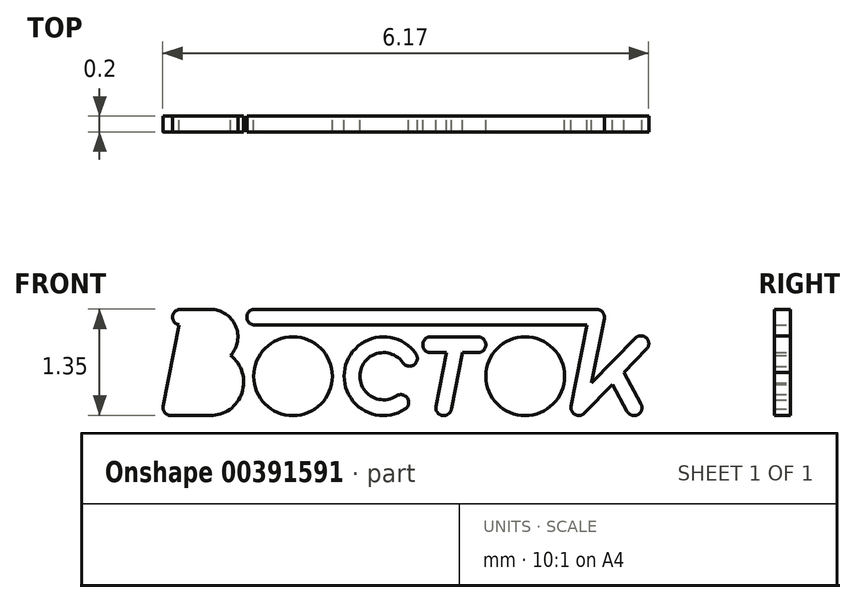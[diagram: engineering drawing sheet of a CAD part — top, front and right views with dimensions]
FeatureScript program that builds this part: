
annotation { "Feature Type Name" : "Feature", "Feature Type Description" : "" }
export const myFeature = defineFeature(function(context is Context, id is Id, definition is map)
    precondition{}
    {
        {
            var Q0;
            Q0=qCreatedBy(makeId("Front.planeOp"),FACE);
            var sketch = newSketch(context, id + "F0", { "sketchPlane" : qUnion([Q0])});
            skArc(sketch, "E0", {"start": v(-21.74, -11.75) * mm, "mid": v(-21.84, -11.84) * mm, "end": v(-21.76, -11.95) * mm});
            skCircle(sketch, "E1", {"center": v(-20.32, -12.6) * mm, "radius": 0.5 * mm});
            skCircle(sketch, "E2", {"center": v(-20.32, -12.6) * mm, "radius": 0.3 * mm});
            skArc(sketch, "E3", {"start": v(-18.75, -12.32) * mm, "mid": v(-19.66, -12.5) * mm, "end": v(-18.9, -13.02) * mm});
            skArc(sketch, "E4", {"start": v(-18.92, -12.43) * mm, "mid": v(-19.46, -12.55) * mm, "end": v(-19, -12.85) * mm});
            skCircle(sketch, "E5", {"center": v(-17.37, -12.6) * mm, "radius": 0.5 * mm});
            skCircle(sketch, "E6", {"center": v(-17.37, -12.6) * mm, "radius": 0.3 * mm});
            skLineSegment(sketch, "E7", {"start": v(-20.32, -12.6) * mm, "end": v(-19.17, -12.6) * mm, "construction": true});
            skLineSegment(sketch, "E8", {"start": v(-18.27, -12.6) * mm, "end": v(-17.37, -12.6) * mm, "construction": true});
            skLineSegment(sketch, "E9", {"start": v(-18.27, -12.6) * mm, "end": v(-19.17, -12.6) * mm, "construction": true});
            skLineSegment(sketch, "E10", {"start": v(-19.17, -12.1) * mm, "end": v(-20.32, -12.1) * mm, "construction": true});
            skLineSegment(sketch, "E11", {"start": v(-20.32, -13.1) * mm, "end": v(-19.17, -13.1) * mm, "construction": true});
            skLineSegment(sketch, "E12", {"start": v(-19.17, -13.1) * mm, "end": v(-17.37, -13.1) * mm, "construction": true});
            skArc(sketch, "E13", {"start": v(-18.57, -12.1) * mm, "mid": v(-18.67, -12.2) * mm, "end": v(-18.57, -12.3) * mm});
            skArc(sketch, "E14", {"start": v(-17.97, -12.3) * mm, "mid": v(-17.87, -12.2) * mm, "end": v(-17.97, -12.1) * mm});
            skArc(sketch, "E15", {"start": v(-18.5, -12.98) * mm, "mid": v(-18.42, -13.1) * mm, "end": v(-18.3, -13.02) * mm});
            skCircle(sketch, "E16", {"center": v(-16.68, -13) * mm, "radius": 0.1 * mm});
            skCircle(sketch, "E17", {"center": v(-15.9, -12.19) * mm, "radius": 0.1 * mm});
            skCircle(sketch, "E18", {"center": v(-15.98, -13) * mm, "radius": 0.1 * mm});
            skArc(sketch, "E19", {"start": v(-18.92, -12.43) * mm, "mid": v(-18.78, -12.46) * mm, "end": v(-18.75, -12.32) * mm});
            skArc(sketch, "E20", {"start": v(-18.9, -13.02) * mm, "mid": v(-18.86, -12.88) * mm, "end": v(-19, -12.85) * mm});
            skArc(sketch, "E21", {"start": v(-21.96, -12.98) * mm, "mid": v(-21.94, -13.07) * mm, "end": v(-21.87, -13.1) * mm});
            skArc(sketch, "E22", {"start": v(-21.37, -12.9) * mm, "mid": v(-21.14, -12.68) * mm, "end": v(-21.37, -12.45) * mm});
            skArc(sketch, "E23", {"start": v(-21.37, -12.25) * mm, "mid": v(-21.22, -12.1) * mm, "end": v(-21.37, -11.95) * mm});
            skArc(sketch, "E24", {"start": v(-21.1, -12.34) * mm, "mid": v(-21.05, -11.96) * mm, "end": v(-21.37, -11.75) * mm});
            skLineSegment(sketch, "E25", {"start": v(-20.32, -13.1) * mm, "end": v(-21.87, -13.1) * mm, "construction": true});
            skLineSegment(sketch, "E26", {"start": v(-21.87, -13.1) * mm, "end": v(-21.37, -13.1) * mm});
            skLineSegment(sketch, "E27", {"start": v(-21.76, -11.95) * mm, "end": v(-21.96, -12.98) * mm});
            skLineSegment(sketch, "E28", {"start": v(-21.74, -11.75) * mm, "end": v(-21.37, -11.75) * mm});
            skLineSegment(sketch, "E29", {"start": v(-20.8, -11.75) * mm, "end": v(-16.46, -11.75) * mm});
            skLineSegment(sketch, "E30", {"start": v(-16.36, -11.87) * mm, "end": v(-16.52, -12.7) * mm});
            skLineSegment(sketch, "E31", {"start": v(-16.52, -12.7) * mm, "end": v(-15.97, -12.12) * mm});
            skLineSegment(sketch, "E32", {"start": v(-15.82, -12.26) * mm, "end": v(-16.11, -12.56) * mm});
            skLineSegment(sketch, "E33", {"start": v(-16.11, -12.56) * mm, "end": v(-15.9, -12.96) * mm});
            skLineSegment(sketch, "E34", {"start": v(-16.07, -13.05) * mm, "end": v(-16.26, -12.7) * mm});
            skLineSegment(sketch, "E35", {"start": v(-16.26, -12.7) * mm, "end": v(-16.61, -13.07) * mm});
            skLineSegment(sketch, "E36", {"start": v(-16.78, -12.98) * mm, "end": v(-16.58, -11.95) * mm});
            skLineSegment(sketch, "E37", {"start": v(-16.58, -11.95) * mm, "end": v(-20.8, -11.95) * mm});
            skArc(sketch, "E38", {"start": v(-20.8, -11.75) * mm, "mid": v(-20.9, -11.85) * mm, "end": v(-20.8, -11.95) * mm});
            skLineSegment(sketch, "E39", {"start": v(-18.57, -12.1) * mm, "end": v(-17.97, -12.1) * mm});
            skLineSegment(sketch, "E40", {"start": v(-18.57, -12.3) * mm, "end": v(-18.37, -12.3) * mm});
            skLineSegment(sketch, "E41", {"start": v(-18.37, -12.3) * mm, "end": v(-18.5, -12.98) * mm});
            skLineSegment(sketch, "E42", {"start": v(-18.3, -13.02) * mm, "end": v(-18.16, -12.3) * mm});
            skLineSegment(sketch, "E43", {"start": v(-18.16, -12.3) * mm, "end": v(-17.97, -12.3) * mm});
            skLineSegment(sketch, "E44", {"start": v(-17.37, -13.1) * mm, "end": v(-16.68, -13.1) * mm, "construction": true});
            skLineSegment(sketch, "E45", {"start": v(-16.68, -13.1) * mm, "end": v(-15.98, -13.1) * mm, "construction": true});
            skLineSegment(sketch, "E46", {"start": v(-16.68, -13) * mm, "end": v(-15.9, -12.19) * mm, "construction": true});
            skArc(sketch, "E47", {"start": v(-16.36, -11.87) * mm, "mid": v(-16.38, -11.79) * mm, "end": v(-16.46, -11.75) * mm});
            skLineSegment(sketch, "E48", {"start": v(-17.97, -12.1) * mm, "end": v(-17.36, -12.1) * mm, "construction": true});
            skLineSegment(sketch, "E49", {"start": v(-18.95, -12.94) * mm, "end": v(-18.84, -12.38) * mm, "construction": true});
            skLineSegment(sketch, "E50", {"start": v(-18.37, -12.3) * mm, "end": v(-18.16, -12.3) * mm, "construction": true});
            skLineSegment(sketch, "E51", {"start": v(-18.57, -12.2) * mm, "end": v(-17.97, -12.2) * mm, "construction": true});
            skPoint(sketch, "E52", {"position": v(-18.27, -12.2) * mm});
            skPoint(sketch, "E53", {"position": v(-18.27, -12.3) * mm});
            skLineSegment(sketch, "E54", {"start": v(-21.75, -12.9) * mm, "end": v(-21.66, -12.45) * mm});
            skLineSegment(sketch, "E55", {"start": v(-21.56, -11.95) * mm, "end": v(-21.37, -11.95) * mm});
            skLineSegment(sketch, "E56", {"start": v(-21.62, -12.25) * mm, "end": v(-21.37, -12.25) * mm});
            skLineSegment(sketch, "E57", {"start": v(-21.37, -12.45) * mm, "end": v(-21.66, -12.45) * mm});
            skLineSegment(sketch, "E58", {"start": v(-21.75, -12.9) * mm, "end": v(-21.37, -12.9) * mm});
            skLineSegment(sketch, "E59.trimOffspring", {"start": v(-21.62, -12.25) * mm, "end": v(-21.56, -11.95) * mm});
            skArc(sketch, "E60.trimOffspring", {"start": v(-21.37, -13.1) * mm, "mid": v(-20.96, -12.81) * mm, "end": v(-21.1, -12.34) * mm});
            skSolve(sketch);
        }
        {
            var Q0;
            Q0=makeQuery(id+"F0.imprint","IMPRINT",FACE,{"disambiguationData":[TD([[makeQuery(id+"F0.imprint","IMPRINT",EDGE,{"derivedFrom":sQuery(id+"F0.wireOp",EDGE,"E1")}),1.0]])]});
            var Q1;
            Q1=makeQuery(id+"F0.imprint","IMPRINT",FACE,{"disambiguationData":[TD([[makeQuery(id+"F0.imprint","IMPRINT",EDGE,{"derivedFrom":sQuery(id+"F0.wireOp",EDGE,"E5")}),1.0]])]});
            var Q2;
            Q2=makeQuery(id+"F0.imprint","IMPRINT",FACE,{"disambiguationData":[TD([[makeQuery(id+"F0.imprint","IMPRINT",EDGE,{"derivedFrom":sQuery(id+"F0.wireOp",EDGE,"E29")}),-1.0]])]});
            var Q3;
            Q3=makeQuery(id+"F0.imprint","IMPRINT",FACE,{"disambiguationData":[TD([[makeQuery(id+"F0.imprint","IMPRINT",EDGE,{"derivedFrom":sQuery(id+"F0.wireOp",EDGE,"E0")}),1.0]])]});
            var Q4;
            Q4=makeQuery(id+"F0.imprint","IMPRINT",FACE,{"disambiguationData":[TD([[makeQuery(id+"F0.imprint","IMPRINT",EDGE,{"derivedFrom":sQuery(id+"F0.wireOp",EDGE,"E13")}),1.0]])]});
            var Q5;
            Q5=makeQuery(id+"F0.imprint","IMPRINT",FACE,{"disambiguationData":[TD([[makeQuery(id+"F0.imprint","IMPRINT",EDGE,{"derivedFrom":sQuery(id+"F0.wireOp",EDGE,"E6")}),1.0]])]});
            var Q6;
            Q6=makeQuery(id+"F0.imprint","IMPRINT",FACE,{"disambiguationData":[TD([[makeQuery(id+"F0.imprint","IMPRINT",EDGE,{"derivedFrom":sQuery(id+"F0.wireOp",EDGE,"E23")}),1.0]])]});
            var Q7;
            Q7=makeQuery(id+"F0.imprint","IMPRINT",FACE,{"disambiguationData":[TD([[makeQuery(id+"F0.imprint","IMPRINT",EDGE,{"derivedFrom":sQuery(id+"F0.wireOp",EDGE,"E22")}),1.0]])]});
            var Q8;
            Q8=makeQuery(id+"F0.imprint","IMPRINT",FACE,{"disambiguationData":[TD([[makeQuery(id+"F0.imprint","IMPRINT",EDGE,{"derivedFrom":sQuery(id+"F0.wireOp",EDGE,"E2")}),1.0]])]});
            var Q9;
            Q9=makeQuery(id+"F0.imprint","IMPRINT",FACE,{"disambiguationData":[TD([[makeQuery(id+"F0.imprint","IMPRINT",EDGE,{"derivedFrom":sQuery(id+"F0.wireOp",EDGE,"E3")}),1.0]])]});
            var Q10;
            {var subQ0=sQuery(id+"F0.wireOp",EDGE,"E18");var subQ1=makeQuery(id+"F0.imprint","INTERSECT",VERTEX,{"derivedFrom":[subQ0,sQuery(id+"F0.wireOp",EDGE,"E33")]});Q10=makeQuery(id+"F0.imprint","IMPRINT",FACE,{"disambiguationData":[TD([[makeQuery(id+"F0.imprint","IMPRINT",EDGE,{"disambiguationData":[TD([[subQ1,-1.0]])],"derivedFrom":subQ0}),1.0]])]});}
            var Q11;
            {var subQ0=sQuery(id+"F0.wireOp",EDGE,"E17");var subQ1=makeQuery(id+"F0.imprint","INTERSECT",VERTEX,{"derivedFrom":[subQ0,sQuery(id+"F0.wireOp",EDGE,"E31")]});Q11=makeQuery(id+"F0.imprint","IMPRINT",FACE,{"disambiguationData":[TD([[makeQuery(id+"F0.imprint","IMPRINT",EDGE,{"disambiguationData":[TD([[subQ1,-1.0]])],"derivedFrom":subQ0}),1.0]])]});}
            var Q12;
            {var subQ0=sQuery(id+"F0.wireOp",EDGE,"E16");var subQ1=makeQuery(id+"F0.imprint","INTERSECT",VERTEX,{"derivedFrom":[subQ0,sQuery(id+"F0.wireOp",EDGE,"E35")]});Q12=makeQuery(id+"F0.imprint","IMPRINT",FACE,{"disambiguationData":[TD([[makeQuery(id+"F0.imprint","IMPRINT",EDGE,{"disambiguationData":[TD([[subQ1,1.0]])],"derivedFrom":subQ0}),1.0]])]});}
            extrude(context, id + "F1", {"entities" : qUnion([Q0, Q1, Q2, Q3, Q4, Q5, Q6, Q7, Q8, Q9, Q10, Q11, Q12]), "depth" : 0.2 * mm});
        }
    });
